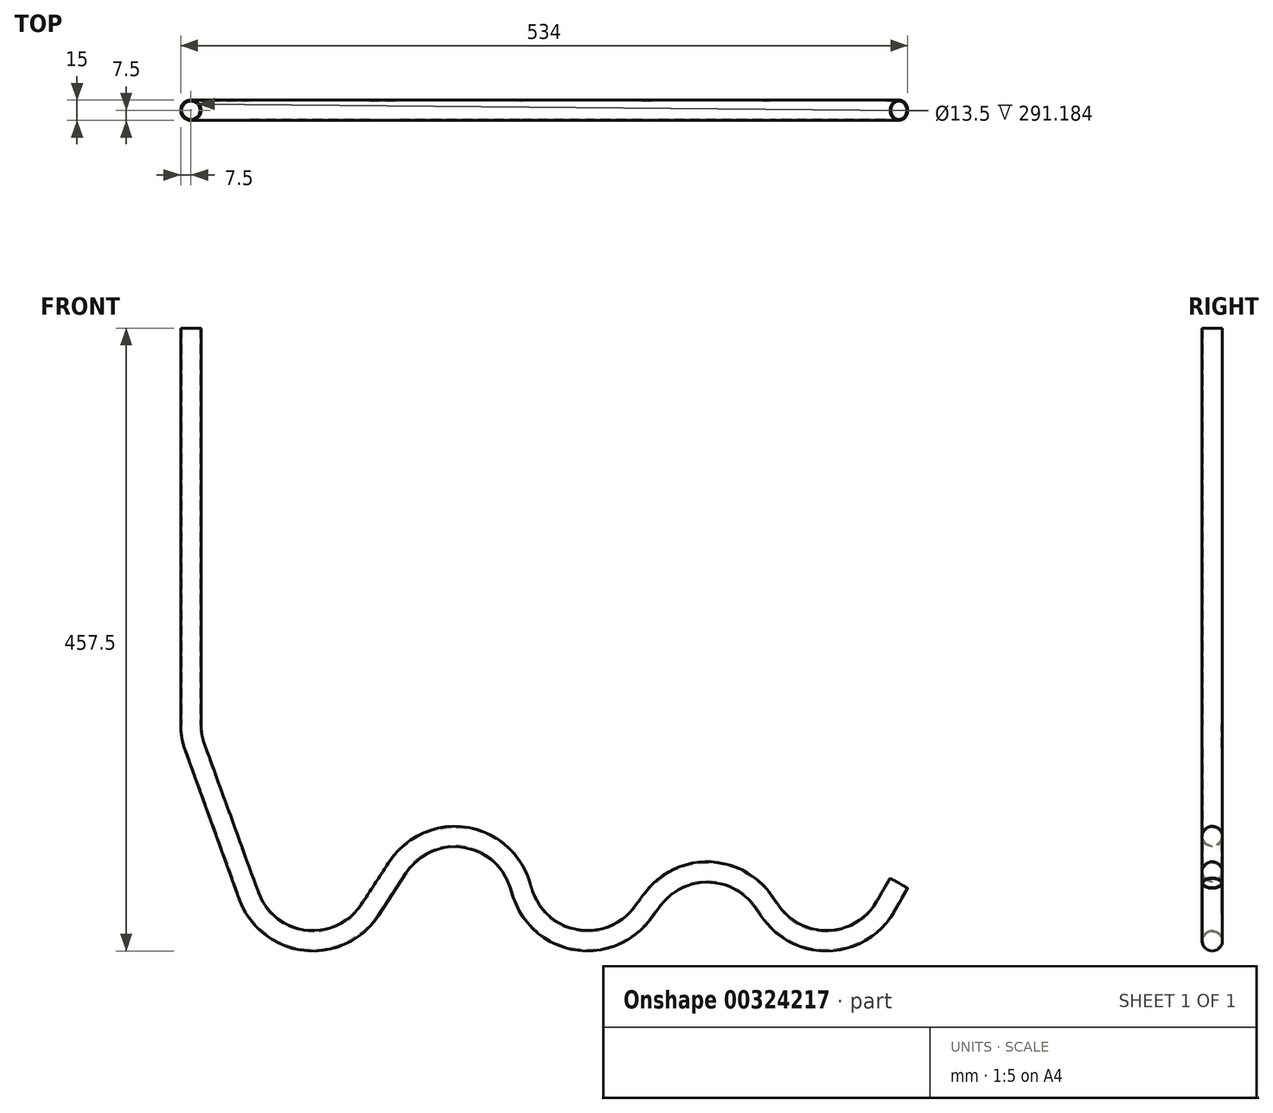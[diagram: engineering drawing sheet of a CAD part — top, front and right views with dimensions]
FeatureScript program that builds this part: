
annotation { "Feature Type Name" : "Feature", "Feature Type Description" : "" }
export const myFeature = defineFeature(function(context is Context, id is Id, definition is map)
    precondition{}
    {
        {
            var Q0;
            Q0=qCreatedBy(makeId("Front.planeOp"),FACE);
            var sketch = newSketch(context, id + "F0", { "sketchPlane" : qUnion([Q0])});
            skLineSegment(sketch, "E0", {"start": v(0, 0) * mm, "end": v(0, -291.18) * mm});
            skLineSegment(sketch, "E1", {"start": v(3.02, -308.28) * mm, "end": v(42.62, -417.1) * mm});
            skLineSegment(sketch, "E2", {"start": v(131.45, -427.37) * mm, "end": v(151.94, -396.04) * mm});
            skLineSegment(sketch, "E3", {"start": v(241.35, -407.99) * mm, "end": v(243.76, -415.41) * mm});
            skLineSegment(sketch, "E4", {"start": v(331.35, -429.96) * mm, "end": v(339.18, -419.5) * mm});
            skLineSegment(sketch, "E5", {"start": v(420.06, -420.63) * mm, "end": v(425.85, -428.83) * mm});
            skLineSegment(sketch, "E6", {"start": v(510, -425) * mm, "end": v(520, -407.68) * mm});
            skPoint(sketch, "E7.visualSharp", {"position": v(0, -300) * mm});
            skArc(sketch, "E7.filletArc", {"start": v(0, -291.18) * mm, "mid": v(0.76, -299.87) * mm, "end": v(3.02, -308.28) * mm});
            skPoint(sketch, "E8.visualSharp", {"position": v(76.78, -510.96) * mm});
            skArc(sketch, "E8.filletArc", {"start": v(42.62, -417.1) * mm, "mid": v(83.87, -449.67) * mm, "end": v(131.45, -427.37) * mm});
            skPoint(sketch, "E9.visualSharp", {"position": v(209.14, -308.57) * mm});
            skArc(sketch, "E9.filletArc", {"start": v(241.35, -407.99) * mm, "mid": v(200.41, -373.84) * mm, "end": v(151.94, -396.04) * mm});
            skPoint(sketch, "E10.visualSharp", {"position": v(273.51, -507.23) * mm});
            skArc(sketch, "E10.filletArc", {"start": v(243.76, -415.41) * mm, "mid": v(283.13, -449.32) * mm, "end": v(331.35, -429.96) * mm});
            skPoint(sketch, "E11.visualSharp", {"position": v(380.4, -364.43) * mm});
            skArc(sketch, "E11.filletArc", {"start": v(420.06, -420.63) * mm, "mid": v(379.91, -399.47) * mm, "end": v(339.18, -419.5) * mm});
            skPoint(sketch, "E12.visualSharp", {"position": v(470.91, -492.7) * mm});
            skArc(sketch, "E12.filletArc", {"start": v(425.85, -428.83) * mm, "mid": v(468.97, -449.95) * mm, "end": v(510, -425) * mm});
            skLineSegment(sketch, "E13", {"start": v(-78.38, -450) * mm, "end": v(600, -450) * mm, "construction": true});
            skLineSegment(sketch, "E14", {"start": v(-325, -300) * mm, "end": v(600, -430) * mm, "construction": true});
            skSolve(sketch);
        }
        {
            var Q0;
            Q0=qCreatedBy(makeId("Top.planeOp"),FACE);
            var sketch = newSketch(context, id + "F1", { "sketchPlane" : qUnion([Q0])});
            skCircle(sketch, "E15", {"center": v(0, 0) * mm, "radius": 7.5 * mm});
            skCircle(sketch, "E16", {"center": v(0, 0) * mm, "radius": 6.75 * mm});
            skSolve(sketch);
        }
        {
            var Q0;
            Q0=makeQuery(id+"F1.imprint","IMPRINT",FACE,{"disambiguationData":[TD([[makeQuery(id+"F1.imprint","IMPRINT",EDGE,{"derivedFrom":sQuery(id+"F1.wireOp",EDGE,"E15")}),1.0]])]});
            var Q1;
            Q1=sQuery(id+"F0.wireOp",EDGE,"E0");
            var Q2;
            Q2=sQuery(id+"F0.wireOp",EDGE,"E7.filletArc");
            var Q3;
            Q3=sQuery(id+"F0.wireOp",EDGE,"E1");
            var Q4;
            Q4=sQuery(id+"F0.wireOp",EDGE,"E8.filletArc");
            var Q5;
            Q5=sQuery(id+"F0.wireOp",EDGE,"E2");
            var Q6;
            Q6=sQuery(id+"F0.wireOp",EDGE,"E9.filletArc");
            var Q7;
            Q7=sQuery(id+"F0.wireOp",EDGE,"E3");
            var Q8;
            Q8=sQuery(id+"F0.wireOp",EDGE,"E10.filletArc");
            var Q9;
            Q9=sQuery(id+"F0.wireOp",EDGE,"E4");
            var Q10;
            Q10=sQuery(id+"F0.wireOp",EDGE,"E11.filletArc");
            var Q11;
            Q11=sQuery(id+"F0.wireOp",EDGE,"E5");
            var Q12;
            Q12=sQuery(id+"F0.wireOp",EDGE,"E12.filletArc");
            var Q13;
            Q13=sQuery(id+"F0.wireOp",EDGE,"E6");
            sweep(context, id + "F2", {"profiles" : qUnion([Q0]), "path" : qUnion([Q1, Q2, Q3, Q4, Q5, Q6, Q7, Q8, Q9, Q10, Q11, Q12, Q13])});
        }
    });
